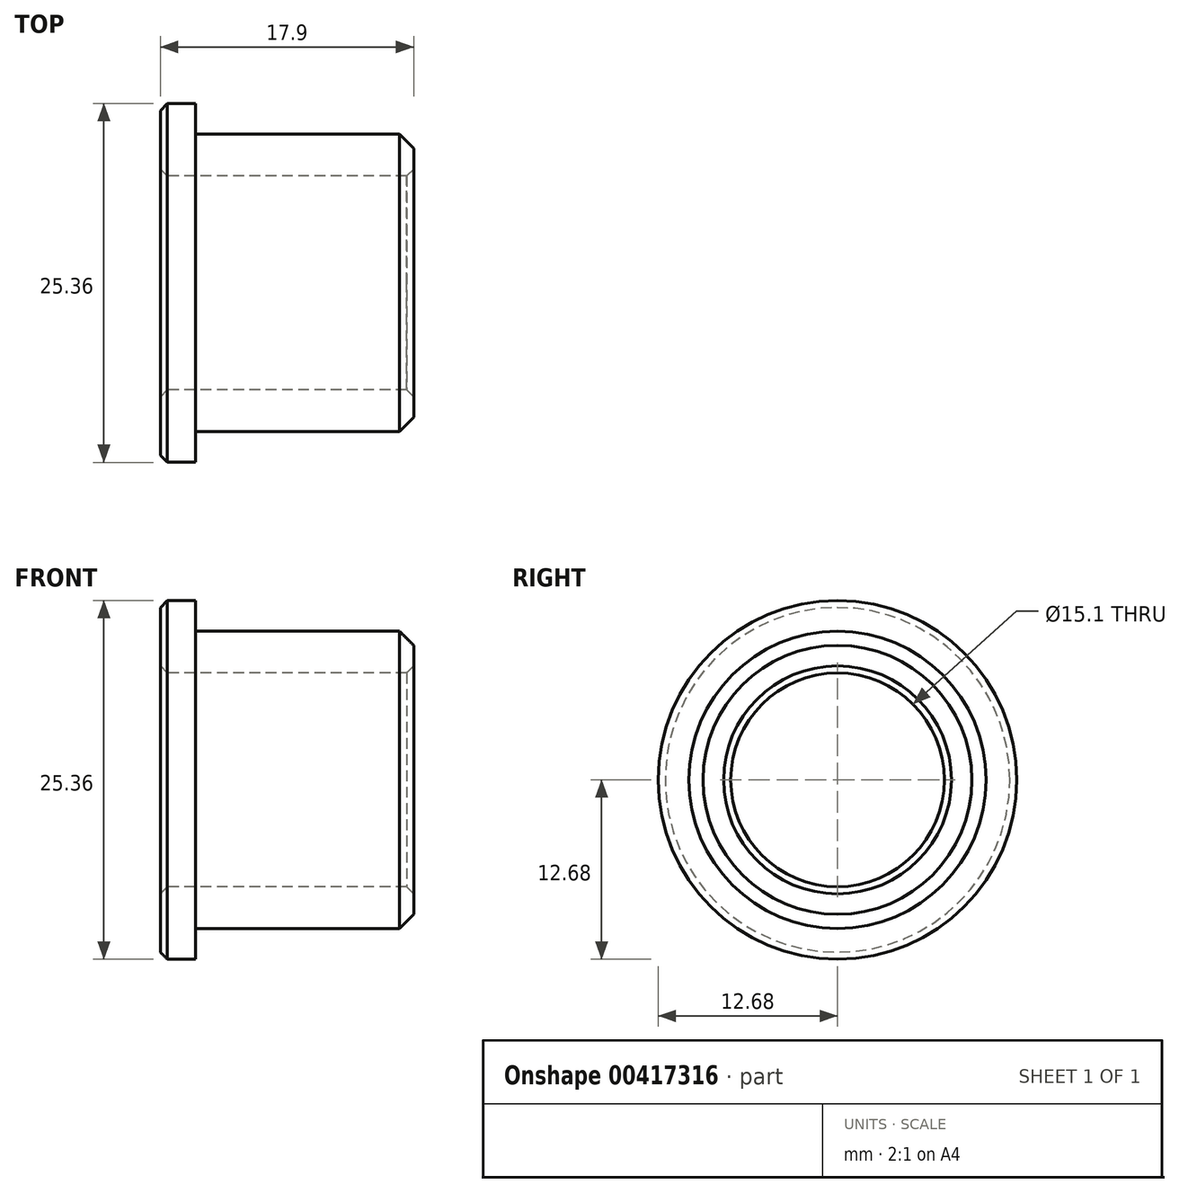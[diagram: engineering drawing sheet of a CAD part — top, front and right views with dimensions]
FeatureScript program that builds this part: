
annotation { "Feature Type Name" : "Feature", "Feature Type Description" : "" }
export const myFeature = defineFeature(function(context is Context, id is Id, definition is map)
    precondition{}
    {
        {
            var Q0;
            Q0=qCreatedBy(makeId("Front.planeOp"),FACE);
            var sketch = newSketch(context, id + "F0", { "sketchPlane" : qUnion([Q0])});
            skLineSegment(sketch, "E0", {"start": v(0, 0) * mm, "end": v(14.58, 0) * mm, "construction": true});
            skLineSegment(sketch, "E1", {"start": v(0, 10.5) * mm, "end": v(0, 12.67) * mm});
            skLineSegment(sketch, "E2", {"start": v(0, 12.67) * mm, "end": v(-2.5, 12.67) * mm});
            skLineSegment(sketch, "E3", {"start": v(-2.5, 12.67) * mm, "end": v(-2.5, 7.55) * mm});
            skLineSegment(sketch, "E4", {"start": v(-2.5, 7.55) * mm, "end": v(15.4, 7.55) * mm});
            skLineSegment(sketch, "E5", {"start": v(15.4, 7.55) * mm, "end": v(15.4, 10.5) * mm});
            skLineSegment(sketch, "E6", {"start": v(15.4, 10.5) * mm, "end": v(0, 10.5) * mm});
            skSolve(sketch);
        }
        {
            var Q0;
            Q0 = qSketchRegion(id + "F0", true);
            var Q1;
            Q1=sQuery(id+"F0.wireOp",EDGE,"E0");
            revolve(context, id + "F1", {"entities" : qUnion([Q0]), "axis" : qUnion([Q1]), "revolveType" : RevolveType.FULL});
        }
        {
            var Q0;
            Q0=makeQuery(id+"F1.opRevolve","SWEPT_EDGE",EDGE,{"disambiguationData":[OSD([sQuery(id+"F0.wireOp",EDGE,"E5"),sQuery(id+"F0.wireOp",EDGE,"E6")])]});
            chamfer(context, id + "F2", {"entities" : qUnion([Q0]), "width" : 1 * mm, "tangentPropagation" : true});
        }
        {
            var Q0;
            Q0=makeQuery(id+"F1.opRevolve","SWEPT_FACE",FACE,{"disambiguationData":[OSD([sQuery(id+"F0.wireOp",EDGE,"E3")])]});
            var Q1;
            Q1=makeQuery(id+"F1.opRevolve","SWEPT_EDGE",EDGE,{"disambiguationData":[OSD([sQuery(id+"F0.wireOp",EDGE,"E4"),sQuery(id+"F0.wireOp",EDGE,"E5")])]});
            chamfer(context, id + "F3", {"entities" : qUnion([Q0, Q1]), "width" : .5 * mm, "tangentPropagation" : true});
        }
    });
